# Revit family: Building-ContenitoriIncasso-GEWISS-24SC-TORRETTE-SCOMPARSA_COPERCHIO_INOX
name_source: partatom
category: Apparecchi elettrici
revit_build: Autodesk Revit 2016 (Build: 20161004_0715(x64)
units: mm (PartAtom-declared; Revit-internal decimal feet)

## family parameters
Condiviso = Sì
Host = Superficie
Mantenere orientamento annotazione = Sì
Punto di calcolo locali = Sì
Quota connettore circolare = Usa diametro
Taglio con vuoti quando caricato = No
Tipo di parte = Normale

## types (1)
- Building-ContenitoriIncasso-GEWISS-24SC-TORRETTE-SCOMPARSA_COPERCHIO_INOX
    Caratteristiche = Halogen free
    Catalogo = BUILDING
    Catalogo Serie = 24SC
    Codice EAN = 8011564759633
    Codice Electrocod = 200
    Coperchio = Inox
    Descrizione = TORRETTA A SCOMPARSA 20P COPERCHIO INOX
    Dim. esterne BxHxP (mm) = 364x98x320
    Glow Wire Test = 850°C
    IDF = 4a87c126-8601-46cb-981d-a9ac82ae8e85
    IDT = 3d95db96-8116-4c07-9f71-f660ca2a642b
    Immagine tipo = GW24612.jpg
    Modello = GW24612
    Modularità interna = 20 moduli SYSTEM
    N. supporti = 4 supporti da 5 moduli System
    Produttore = GEWISS S.p.A.
    Prospetto di default = 1219 mm
    SEO = Torretta
    Scheda Tecnica = https://www.gewiss.com
    TIPO = Torrette a Scomparsa coperchi inox_GENERICO : GW24612
    Temperatura di impiego = -5 +45 °C
    URL = https://www.gewiss.com
    Versione file RFA = 19.0

## geometry (parser evidence)
native form markers: Blend x2, Sweep x1
no freeform markers — native parametric forms only
